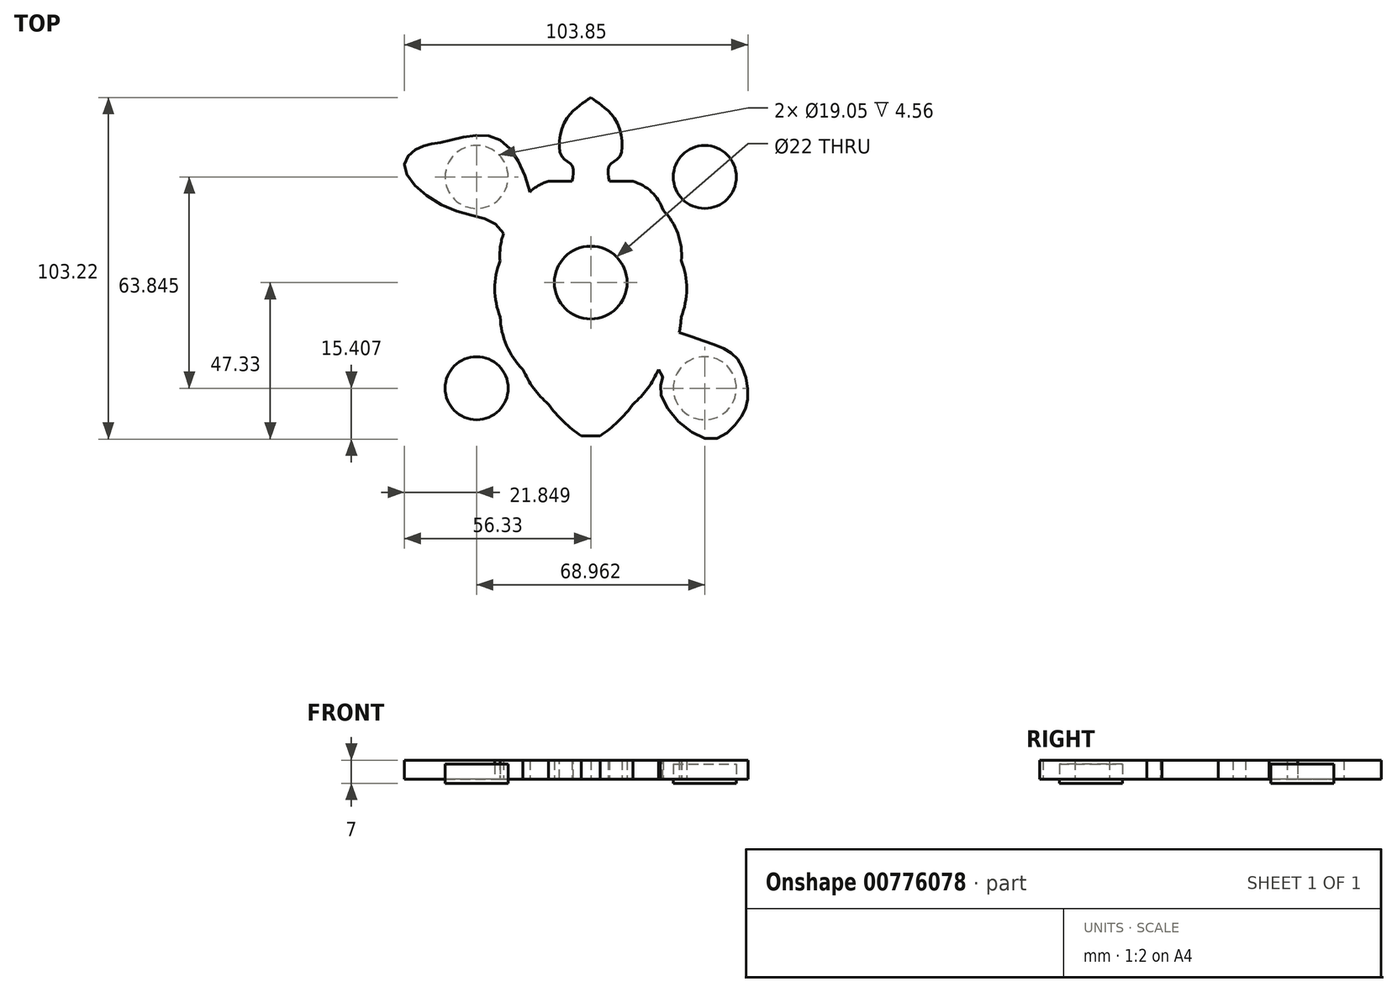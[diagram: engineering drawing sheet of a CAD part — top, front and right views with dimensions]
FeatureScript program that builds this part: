
annotation { "Feature Type Name" : "Feature", "Feature Type Description" : "" }
export const myFeature = defineFeature(function(context is Context, id is Id, definition is map)
    precondition{}
    {
        {
            var Q0;
            Q0=qCreatedBy(makeId("Top.planeOp"),FACE);
            var sketch = newSketch(context, id + "F0", { "sketchPlane" : qUnion([Q0])});
            skCircle(sketch, "E0", {"center": v(0, 0) * mm, "radius": 11 * mm});
            skCircle(sketch, "E1", {"center": v(-34.48, 31.92) * mm, "radius": 9.53 * mm});
            skPoint(sketch, "E2.orphan", {"position": v(-34.48, -31.92) * mm});
            skPoint(sketch, "E3.orphan", {"position": v(34.48, 31.92) * mm});
            skPoint(sketch, "E4.orphan", {"position": v(34.48, -31.92) * mm});
            skCircle(sketch, "E5.MirrorC", {"center": v(34.48, 31.92) * mm, "radius": 9.53 * mm});
            skCircle(sketch, "E6.MirrorC", {"center": v(-34.48, -31.92) * mm, "radius": 9.53 * mm});
            skCircle(sketch, "E7.MirrorC", {"center": v(34.48, -31.92) * mm, "radius": 9.53 * mm});
            skLineSegment(sketch, "E8", {"start": v(0, 30.62) * mm, "end": v(-12.8, 30.62) * mm});
            skLineSegment(sketch, "E9", {"start": v(-2.84, -46.36) * mm, "end": v(0, -46.36) * mm});
            skArc(sketch, "E10", {"start": v(-12.8, 30.62) * mm, "mid": v(-18.39, 27.36) * mm, "end": v(-21.88, 21.92) * mm});
            skArc(sketch, "E11", {"start": v(-21.88, 21.92) * mm, "mid": v(-26.32, 14.85) * mm, "end": v(-27.42, 6.57) * mm});
            skArc(sketch, "E12", {"start": v(-27.42, 6.57) * mm, "mid": v(-29, -1.93) * mm, "end": v(-27.34, -10.42) * mm});
            skArc(sketch, "E13", {"start": v(-27.34, -10.42) * mm, "mid": v(-25.43, -19) * mm, "end": v(-20.46, -26.25) * mm});
            skArc(sketch, "E14", {"start": v(-20.46, -26.25) * mm, "mid": v(-17.24, -31.97) * mm, "end": v(-12.8, -36.78) * mm});
            skArc(sketch, "E15", {"start": v(-12.8, -36.78) * mm, "mid": v(-8.24, -42.01) * mm, "end": v(-2.84, -46.36) * mm});
            skLineSegment(sketch, "E16.MirrorCS", {"start": v(0, 30.62) * mm, "end": v(12.8, 30.62) * mm});
            skArc(sketch, "E17.MirrorCS", {"start": v(12.8, 30.62) * mm, "mid": v(18.39, 27.36) * mm, "end": v(21.88, 21.92) * mm});
            skArc(sketch, "E18.MirrorCS", {"start": v(21.88, 21.92) * mm, "mid": v(26.32, 14.85) * mm, "end": v(27.42, 6.57) * mm});
            skArc(sketch, "E19.MirrorCS", {"start": v(27.42, 6.57) * mm, "mid": v(29, -1.93) * mm, "end": v(27.34, -10.42) * mm});
            skArc(sketch, "E20.MirrorCS", {"start": v(27.34, -10.42) * mm, "mid": v(25.43, -19) * mm, "end": v(20.46, -26.25) * mm});
            skArc(sketch, "E21.MirrorCS", {"start": v(20.46, -26.25) * mm, "mid": v(17.24, -31.97) * mm, "end": v(12.8, -36.78) * mm});
            skArc(sketch, "E22.MirrorCS", {"start": v(12.8, -36.78) * mm, "mid": v(8.24, -42.01) * mm, "end": v(2.84, -46.36) * mm});
            skLineSegment(sketch, "E23.MirrorCS", {"start": v(2.84, -46.36) * mm, "end": v(0, -46.36) * mm});
            skFitSpline(sketch, "E24", {"points": [v(-18.39, 27.36) * mm, v(-29.36, 44.02) * mm, v(-44.02, 42.62) * mm, v(-51.46, 41) * mm, v(-56.32, 35.02) * mm, v(-41.46, 21.92) * mm, v(-26.32, 14.85) * mm], "startDerivative": vector(-28.49, 118.46) * mm, "endDerivative": vector(42.34, -85.6) * mm});
            skFitSpline(sketch, "E25", {"points": [v(-26.75, -15.04) * mm, v(-39.4, -19.6) * mm, v(-44.95, -23.9) * mm, v(-47.5, -34.36) * mm, v(-44.48, -42.04) * mm, v(-34.75, -47.17) * mm, v(-21, -32.5) * mm, v(-20.46, -26.25) * mm], "startDerivative": vector(-86.65, -33.33) * mm, "endDerivative": vector(71.2, 56.58) * mm});
            skFitSpline(sketch, "E26", {"points": [v(-5.63, 30.62) * mm, v(-5.63, 35.24) * mm, v(-8.84, 38.3) * mm, v(-7.85, 48.53) * mm, v(-3.03, 53.75) * mm, v(0, 55.9) * mm], "startDerivative": vector(5.32, 26.43) * mm, "endDerivative": vector(17.69, 12.24) * mm});
            skFitSpline(sketch, "E27.MirrorCS", {"points": [v(18.39, 27.36) * mm, v(29.36, 44.02) * mm, v(44.02, 42.62) * mm, v(51.46, 41) * mm, v(56.32, 35.02) * mm, v(41.46, 21.92) * mm, v(26.32, 14.85) * mm], "startDerivative": vector(28.49, 118.46) * mm, "endDerivative": vector(-42.34, -85.6) * mm});
            skFitSpline(sketch, "E28.MirrorCS", {"points": [v(5.63, 30.62) * mm, v(5.63, 35.24) * mm, v(8.84, 38.3) * mm, v(7.85, 48.53) * mm, v(3.03, 53.75) * mm, v(0, 55.9) * mm], "startDerivative": vector(-5.32, 26.43) * mm, "endDerivative": vector(-17.69, 12.24) * mm});
            skFitSpline(sketch, "E29.MirrorCS", {"points": [v(26.75, -15.04) * mm, v(39.4, -19.6) * mm, v(44.95, -23.9) * mm, v(47.5, -34.36) * mm, v(44.48, -42.04) * mm, v(34.75, -47.17) * mm, v(21, -32.5) * mm, v(20.46, -26.25) * mm], "startDerivative": vector(86.65, -33.33) * mm, "endDerivative": vector(-71.2, 56.58) * mm});
            skSolve(sketch);
        }
        {
            var Q0;
            {var subQ3=sQuery(id+"F0.wireOp",EDGE,"E26");Q0=makeQuery(id+"F0.imprint","IMPRINT",FACE,{"disambiguationData":[TD([[makeQuery(id+"F0.imprint","IMPRINT",EDGE,{"derivedFrom":subQ3}),-1.0]])]});}
            var Q1;
            Q1=makeQuery(id+"F0.imprint","IMPRINT",FACE,{"disambiguationData":[TD([[makeQuery(id+"F0.imprint","IMPRINT",EDGE,{"derivedFrom":sQuery(id+"F0.wireOp",EDGE,"E1")}),-1.0]])]});
            var Q2;
            Q2=makeQuery(id+"F0.imprint","IMPRINT",FACE,{"disambiguationData":[TD([[makeQuery(id+"F0.imprint","IMPRINT",EDGE,{"derivedFrom":sQuery(id+"F0.wireOp",EDGE,"E0")}),-1.0]])]});
            var Q3;
            Q3=makeQuery(id+"F0.imprint","IMPRINT",FACE,{"disambiguationData":[TD([[makeQuery(id+"F0.imprint","IMPRINT",EDGE,{"derivedFrom":sQuery(id+"F0.wireOp",EDGE,"E5.MirrorC")}),1.0]])]});
            var Q4;
            Q4=makeQuery(id+"F0.imprint","IMPRINT",FACE,{"disambiguationData":[TD([[makeQuery(id+"F0.imprint","IMPRINT",EDGE,{"derivedFrom":sQuery(id+"F0.wireOp",EDGE,"E7.MirrorC")}),-1.0]])]});
            var Q5;
            Q5=makeQuery(id+"F0.imprint","IMPRINT",FACE,{"disambiguationData":[TD([[makeQuery(id+"F0.imprint","IMPRINT",EDGE,{"derivedFrom":sQuery(id+"F0.wireOp",EDGE,"E6.MirrorC")}),1.0]])]});
            extrude(context, id + "F1", {"entities" : qUnion([Q0, Q1, Q2, Q3, Q4, Q5]), "depth" : 4.56 * mm, "offsetDistance" : 25.4 * mm});
        }
        {
            var Q0;
            Q0=makeQuery(id+"F1.opExtrude","CAP_FACE",FACE,{"disambiguationData":[OSD([sQuery(id+"F0.wireOp",EDGE,"E0"),sQuery(id+"F0.wireOp",EDGE,"E1"),sQuery(id+"F0.wireOp",EDGE,"E5.MirrorC"),sQuery(id+"F0.wireOp",EDGE,"E6.MirrorC"),sQuery(id+"F0.wireOp",EDGE,"E7.MirrorC"),sQuery(id+"F0.wireOp",EDGE,"E8"),sQuery(id+"F0.wireOp",EDGE,"E9"),sQuery(id+"F0.wireOp",EDGE,"E10"),sQuery(id+"F0.wireOp",EDGE,"E11"),sQuery(id+"F0.wireOp",EDGE,"E12"),sQuery(id+"F0.wireOp",EDGE,"E13"),sQuery(id+"F0.wireOp",EDGE,"E14"),sQuery(id+"F0.wireOp",EDGE,"E15"),sQuery(id+"F0.wireOp",EDGE,"E16.MirrorCS"),sQuery(id+"F0.wireOp",EDGE,"E17.MirrorCS"),sQuery(id+"F0.wireOp",EDGE,"E18.MirrorCS"),sQuery(id+"F0.wireOp",EDGE,"E19.MirrorCS"),sQuery(id+"F0.wireOp",EDGE,"E20.MirrorCS"),sQuery(id+"F0.wireOp",EDGE,"E21.MirrorCS"),sQuery(id+"F0.wireOp",EDGE,"E22.MirrorCS"),sQuery(id+"F0.wireOp",EDGE,"E23.MirrorCS"),sQuery(id+"F0.wireOp",EDGE,"E24"),sQuery(id+"F0.wireOp",EDGE,"E25"),sQuery(id+"F0.wireOp",EDGE,"E26"),sQuery(id+"F0.wireOp",EDGE,"E27.MirrorCS"),sQuery(id+"F0.wireOp",EDGE,"E28.MirrorCS"),sQuery(id+"F0.wireOp",EDGE,"E29.MirrorCS")])],"isStart":true});
            var sketch = newSketch(context, id + "F2", { "sketchPlane" : qUnion([Q0])});
            skCircle(sketch, "E30", {"center": v(-34.48, 31.92) * mm, "radius": 9.53 * mm});
            skCircle(sketch, "E31", {"center": v(0, 0) * mm, "radius": 11 * mm});
            skCircle(sketch, "E32.MirrorC", {"center": v(34.48, 31.92) * mm, "radius": 9.53 * mm});
            skCircle(sketch, "E33.MirrorC", {"center": v(-34.48, -31.92) * mm, "radius": 9.53 * mm});
            skCircle(sketch, "E34.MirrorC", {"center": v(34.48, -31.92) * mm, "radius": 9.53 * mm});
            skSolve(sketch);
        }
        {
            var Q0;
            Q0=makeQuery(id+"F2.imprint","IMPRINT",FACE,{"disambiguationData":[TD([[makeQuery(id+"F2.imprint","IMPRINT",EDGE,{"derivedFrom":sQuery(id+"F2.wireOp",EDGE,"E30")}),1.0]])]});
            var Q1;
            Q1=makeQuery(id+"F2.imprint","IMPRINT",FACE,{"disambiguationData":[TD([[makeQuery(id+"F2.imprint","IMPRINT",EDGE,{"derivedFrom":sQuery(id+"F2.wireOp",EDGE,"E32.MirrorC")}),-1.0]])]});
            var Q2;
            Q2=makeQuery(id+"F2.imprint","IMPRINT",FACE,{"disambiguationData":[TD([[makeQuery(id+"F2.imprint","IMPRINT",EDGE,{"derivedFrom":sQuery(id+"F2.wireOp",EDGE,"E33.MirrorC")}),-1.0]])]});
            var Q3;
            Q3=makeQuery(id+"F2.imprint","IMPRINT",FACE,{"disambiguationData":[TD([[makeQuery(id+"F2.imprint","IMPRINT",EDGE,{"derivedFrom":sQuery(id+"F2.wireOp",EDGE,"E34.MirrorC")}),1.0]])]});
            var Q4;
            Q4=makeQuery(id+"F2.imprint","IMPRINT",FACE,{"disambiguationData":[TD([[makeQuery(id+"F2.imprint","IMPRINT",EDGE,{"derivedFrom":sQuery(id+"F2.wireOp",EDGE,"E30")}),-1.0]])]});
            extrude(context, id + "F3", {"entities" : qUnion([Q0, Q1, Q2, Q3, Q4]), "operationType" : NewBodyOperationType.ADD, "depth" : 1.22 * mm, "offsetDistance" : 25.4 * mm});
        }
        {
            var Q0;
            Q0=makeQuery(id+"F1.opExtrude","CAP_FACE",FACE,{"disambiguationData":[OSD([sQuery(id+"F0.wireOp",EDGE,"E0"),sQuery(id+"F0.wireOp",EDGE,"E1"),sQuery(id+"F0.wireOp",EDGE,"E5.MirrorC"),sQuery(id+"F0.wireOp",EDGE,"E6.MirrorC"),sQuery(id+"F0.wireOp",EDGE,"E7.MirrorC"),sQuery(id+"F0.wireOp",EDGE,"E8"),sQuery(id+"F0.wireOp",EDGE,"E9"),sQuery(id+"F0.wireOp",EDGE,"E10"),sQuery(id+"F0.wireOp",EDGE,"E11"),sQuery(id+"F0.wireOp",EDGE,"E12"),sQuery(id+"F0.wireOp",EDGE,"E13"),sQuery(id+"F0.wireOp",EDGE,"E14"),sQuery(id+"F0.wireOp",EDGE,"E15"),sQuery(id+"F0.wireOp",EDGE,"E16.MirrorCS"),sQuery(id+"F0.wireOp",EDGE,"E17.MirrorCS"),sQuery(id+"F0.wireOp",EDGE,"E18.MirrorCS"),sQuery(id+"F0.wireOp",EDGE,"E19.MirrorCS"),sQuery(id+"F0.wireOp",EDGE,"E20.MirrorCS"),sQuery(id+"F0.wireOp",EDGE,"E21.MirrorCS"),sQuery(id+"F0.wireOp",EDGE,"E22.MirrorCS"),sQuery(id+"F0.wireOp",EDGE,"E23.MirrorCS"),sQuery(id+"F0.wireOp",EDGE,"E24"),sQuery(id+"F0.wireOp",EDGE,"E25"),sQuery(id+"F0.wireOp",EDGE,"E26"),sQuery(id+"F0.wireOp",EDGE,"E27.MirrorCS"),sQuery(id+"F0.wireOp",EDGE,"E28.MirrorCS"),sQuery(id+"F0.wireOp",EDGE,"E29.MirrorCS")])],"isStart":false});
            var sketch = newSketch(context, id + "F4", { "sketchPlane" : qUnion([Q0])});
            skCircle(sketch, "E35", {"center": v(-34.48, 31.92) * mm, "radius": 9.53 * mm});
            skCircle(sketch, "E36", {"center": v(0, 0) * mm, "radius": 11 * mm});
            skCircle(sketch, "E37.MirrorC", {"center": v(34.48, 31.92) * mm, "radius": 9.53 * mm});
            skCircle(sketch, "E38.MirrorC", {"center": v(-34.48, -31.92) * mm, "radius": 9.53 * mm});
            skCircle(sketch, "E39.MirrorC", {"center": v(34.48, -31.92) * mm, "radius": 9.53 * mm});
            skSolve(sketch);
        }
        {
            var Q0;
            Q0=makeQuery(id+"F4.imprint","IMPRINT",FACE,{"disambiguationData":[TD([[makeQuery(id+"F4.imprint","IMPRINT",EDGE,{"derivedFrom":sQuery(id+"F4.wireOp",EDGE,"E35")}),1.0]])]});
            var Q1;
            Q1=makeQuery(id+"F4.imprint","IMPRINT",FACE,{"disambiguationData":[TD([[makeQuery(id+"F4.imprint","IMPRINT",EDGE,{"derivedFrom":sQuery(id+"F4.wireOp",EDGE,"E37.MirrorC")}),-1.0]])]});
            var Q2;
            Q2=makeQuery(id+"F4.imprint","IMPRINT",FACE,{"disambiguationData":[TD([[makeQuery(id+"F4.imprint","IMPRINT",EDGE,{"derivedFrom":sQuery(id+"F4.wireOp",EDGE,"E38.MirrorC")}),-1.0]])]});
            var Q3;
            Q3=makeQuery(id+"F4.imprint","IMPRINT",FACE,{"disambiguationData":[TD([[makeQuery(id+"F4.imprint","IMPRINT",EDGE,{"derivedFrom":sQuery(id+"F4.wireOp",EDGE,"E39.MirrorC")}),1.0]])]});
            var Q4;
            Q4=makeQuery(id+"F4.imprint","IMPRINT",FACE,{"disambiguationData":[TD([[makeQuery(id+"F4.imprint","IMPRINT",EDGE,{"derivedFrom":sQuery(id+"F4.wireOp",EDGE,"E35")}),-1.0]])]});
            extrude(context, id + "F5", {"entities" : qUnion([Q0, Q1, Q2, Q3, Q4]), "operationType" : NewBodyOperationType.ADD, "depth" : 1.22 * mm, "offsetDistance" : 25.4 * mm});
        }
    });
